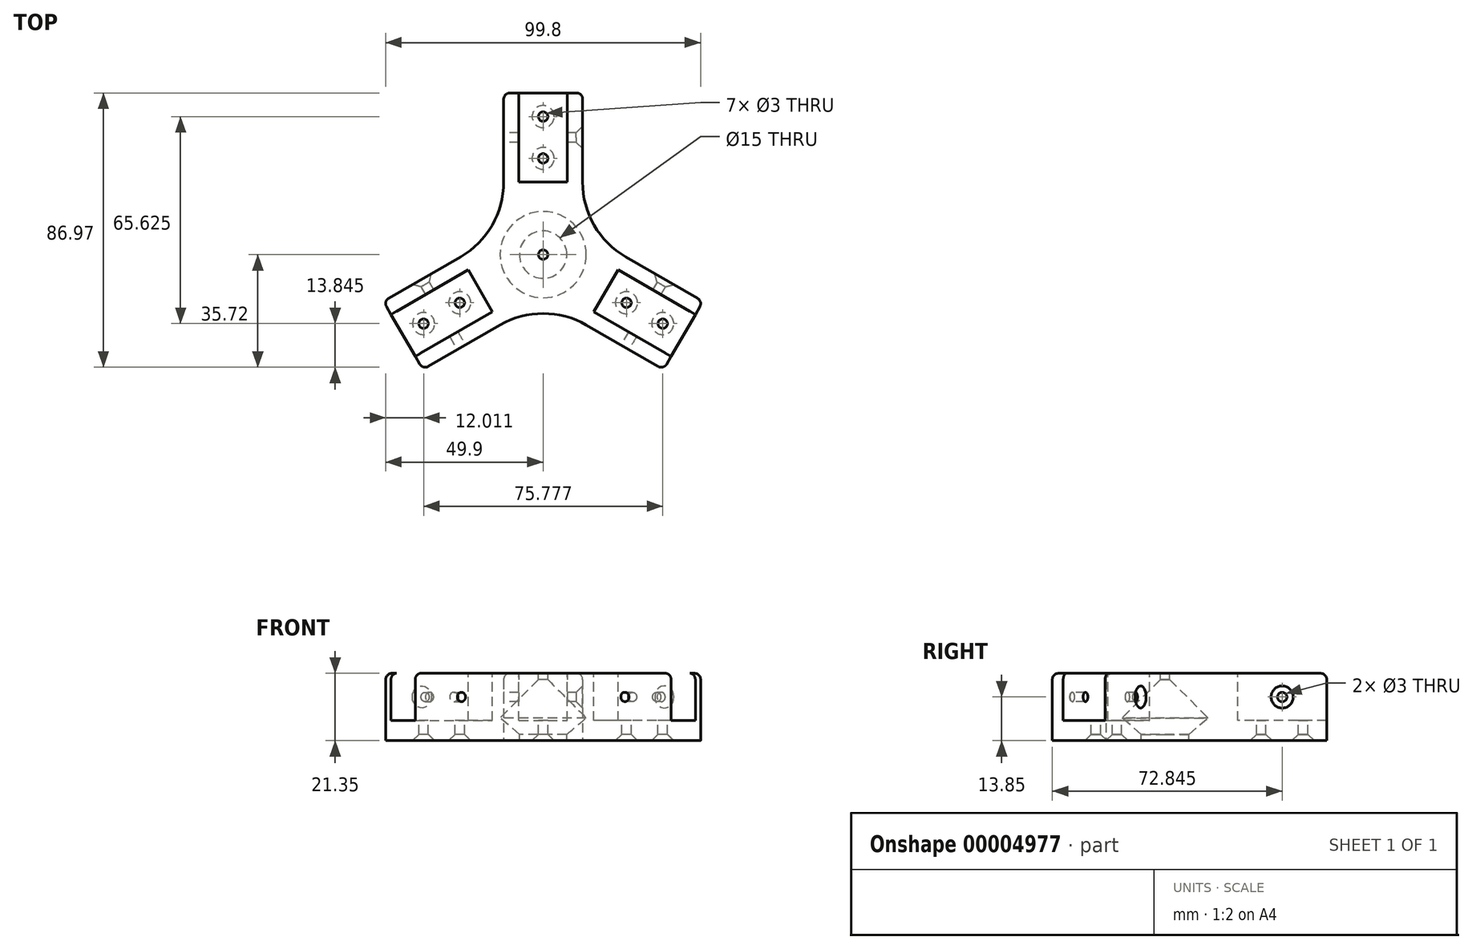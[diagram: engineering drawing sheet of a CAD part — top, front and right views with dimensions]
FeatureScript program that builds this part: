
annotation { "Feature Type Name" : "Feature", "Feature Type Description" : "" }
export const myFeature = defineFeature(function(context is Context, id is Id, definition is map)
    precondition{}
    {
        {
            var Q0;
            Q0=qCreatedBy(makeId("Top.planeOp"),FACE);
            var sketch = newSketch(context, id + "F0", { "sketchPlane" : qUnion([Q0])});
            skCircle(sketch, "E0", {"center": v(0, 0) * mm, "radius": 6.25 * mm, "construction": true});
            skLineSegment(sketch, "E1", {"start": v(0, 0) * mm, "end": v(0, 51.25) * mm, "construction": true});
            skLineSegment(sketch, "E2", {"start": v(-12.5, 51.25) * mm, "end": v(12.5, 51.25) * mm});
            skLineSegment(sketch, "E3", {"start": v(0, 0) * mm, "end": v(44.38, -25.62) * mm, "construction": true});
            skLineSegment(sketch, "E4", {"start": v(12.5, 51.25) * mm, "end": v(12.5, 23) * mm});
            skLineSegment(sketch, "E5", {"start": v(38.13, -36.45) * mm, "end": v(50.63, -14.8) * mm});
            skLineSegment(sketch, "E6", {"start": v(50.63, -14.8) * mm, "end": v(26.17, -0.67) * mm});
            skArc(sketch, "E7", {"start": v(12.5, 23) * mm, "mid": v(16.16, 9.33) * mm, "end": v(26.17, -0.67) * mm});
            skPoint(sketch, "E8", {"position": v(0, 6.25) * mm});
            skLineSegment(sketch, "E9.1.0", {"start": v(-50.63, -14.8) * mm, "end": v(-26.17, -0.67) * mm});
            skArc(sketch, "E9.1.1", {"start": v(-26.17, -0.67) * mm, "mid": v(-16.16, 9.33) * mm, "end": v(-12.5, 23) * mm});
            skLineSegment(sketch, "E9.1.2", {"start": v(-12.5, 51.25) * mm, "end": v(-12.5, 23) * mm});
            skLineSegment(sketch, "E9.2.0", {"start": v(38.13, -36.45) * mm, "end": v(13.67, -22.33) * mm});
            skArc(sketch, "E9.2.1", {"start": v(13.67, -22.33) * mm, "mid": v(0, -18.66) * mm, "end": v(-13.67, -22.33) * mm});
            skLineSegment(sketch, "E9.2.2", {"start": v(-38.13, -36.45) * mm, "end": v(-13.67, -22.33) * mm});
            skLineSegment(sketch, "E10", {"start": v(-50.63, -14.8) * mm, "end": v(-38.13, -36.45) * mm});
            skLineSegment(sketch, "E11", {"start": v(-12.5, 23) * mm, "end": v(12.5, 23) * mm, "construction": true});
            skCircle(sketch, "E12", {"center": v(0, 0) * mm, "radius": 13.66 * mm});
            skSolve(sketch);
        }
        {
            var Q0;
            Q0=qSketchRegion(id+"F0",true);
            extrude(context, id + "F1", {"entities" : qUnion([Q0]), "depth" : 21.35 * mm, "offsetDistance" : 25 * mm});
        }
        {
            var Q0;
            Q0=makeQuery(id+"F1.opExtrude","CAP_FACE",FACE,{"disambiguationData":[OSD([sQuery(id+"F0.wireOp",EDGE,"E0"),sQuery(id+"F0.wireOp",EDGE,"E2"),sQuery(id+"F0.wireOp",EDGE,"E4"),sQuery(id+"F0.wireOp",EDGE,"E5"),sQuery(id+"F0.wireOp",EDGE,"E6"),sQuery(id+"F0.wireOp",EDGE,"E7"),sQuery(id+"F0.wireOp",EDGE,"E9.1.0"),sQuery(id+"F0.wireOp",EDGE,"E9.1.1"),sQuery(id+"F0.wireOp",EDGE,"E9.1.2"),sQuery(id+"F0.wireOp",EDGE,"E9.2.0"),sQuery(id+"F0.wireOp",EDGE,"E9.2.1"),sQuery(id+"F0.wireOp",EDGE,"E9.2.2"),sQuery(id+"F0.wireOp",EDGE,"E10")])],"isStart":false});
            var sketch = newSketch(context, id + "F2", { "sketchPlane" : qUnion([Q0])});
            skLineSegment(sketch, "E13", {"start": v(0, 0) * mm, "end": v(0, 51.25) * mm, "construction": true});
            skLineSegment(sketch, "E14", {"start": v(-12.5, 23) * mm, "end": v(12.5, 23) * mm, "construction": true});
            skLineSegment(sketch, "E15.bottom", {"start": v(-7.68, 51.25) * mm, "end": v(7.67, 51.25) * mm});
            skLineSegment(sketch, "E15.top", {"start": v(-7.68, 23) * mm, "end": v(7.67, 23) * mm});
            skLineSegment(sketch, "E15.left", {"start": v(-7.68, 51.25) * mm, "end": v(-7.68, 23) * mm});
            skLineSegment(sketch, "E15.right", {"start": v(7.67, 51.25) * mm, "end": v(7.67, 23) * mm});
            skLineSegment(sketch, "E16.1.0", {"start": v(-48.22, -18.98) * mm, "end": v(-23.76, -4.85) * mm});
            skLineSegment(sketch, "E16.1.1", {"start": v(-40.55, -32.27) * mm, "end": v(-48.22, -18.98) * mm});
            skLineSegment(sketch, "E16.1.2", {"start": v(-40.55, -32.27) * mm, "end": v(-16.08, -18.15) * mm});
            skLineSegment(sketch, "E16.1.3", {"start": v(-16.08, -18.15) * mm, "end": v(-23.76, -4.85) * mm});
            skLineSegment(sketch, "E16.2.0", {"start": v(40.55, -32.27) * mm, "end": v(16.08, -18.15) * mm});
            skLineSegment(sketch, "E16.2.1", {"start": v(48.22, -18.98) * mm, "end": v(40.55, -32.27) * mm});
            skLineSegment(sketch, "E16.2.2", {"start": v(48.22, -18.98) * mm, "end": v(23.76, -4.85) * mm});
            skLineSegment(sketch, "E16.2.3", {"start": v(23.76, -4.85) * mm, "end": v(16.08, -18.15) * mm});
            skPoint(sketch, "E16.center", {"position": v(0, 0) * mm});
            skSolve(sketch);
        }
        {
            var Q0;
            Q0=qSketchRegion(id+"F2",true);
            extrude(context, id + "F3", {"entities" : qUnion([Q0]), "operationType" : NewBodyOperationType.REMOVE, "oppositeDirection" : true, "depth" : 15 * mm, "offsetDistance" : 25 * mm});
        }
        {
            var Q0;
            Q0=makeQuery(id+"F3.boolean.opBoolean","COPY",FACE,{"derivedFrom":makeQuery(id+"F3.opExtrude","CAP_FACE",FACE,{"disambiguationData":[OSD([sQuery(id+"F2.wireOp",EDGE,"E15.bottom"),sQuery(id+"F2.wireOp",EDGE,"E15.top"),sQuery(id+"F2.wireOp",EDGE,"E15.left"),sQuery(id+"F2.wireOp",EDGE,"E15.right")])],"isStart":false})});
            var sketch = newSketch(context, id + "F4", { "sketchPlane" : qUnion([Q0])});
            skLineSegment(sketch, "E17", {"start": v(0, 51.25) * mm, "end": v(0, 23) * mm, "construction": true});
            skCircle(sketch, "E18", {"center": v(0, 43.75) * mm, "radius": 1.5 * mm});
            skCircle(sketch, "E19", {"center": v(0, 30.5) * mm, "radius": 1.5 * mm});
            skCircle(sketch, "E20.1.0", {"center": v(-37.89, -21.87) * mm, "radius": 1.5 * mm});
            skCircle(sketch, "E20.1.1", {"center": v(-26.41, -15.25) * mm, "radius": 1.5 * mm});
            skCircle(sketch, "E20.2.0", {"center": v(37.89, -21.87) * mm, "radius": 1.5 * mm});
            skCircle(sketch, "E20.2.1", {"center": v(26.41, -15.25) * mm, "radius": 1.5 * mm});
            skPoint(sketch, "E20.center", {"position": v(0, 0) * mm});
            skSolve(sketch);
        }
        {
            var Q0;
            Q0=qSketchRegion(id+"F4",true);
            extrude(context, id + "F5", {"entities" : qUnion([Q0]), "operationType" : NewBodyOperationType.REMOVE, "endBound" : BoundingType.THROUGH_ALL, "oppositeDirection" : true, "depth" : 25 * mm});
        }
        {
            var Q0;
            {var subQ0=sQuery(id+"F0.wireOp",EDGE,"E2");var subQ1=sQuery(id+"F0.wireOp",EDGE,"E9.1.2");Q0=makeQuery(id+"F3.boolean.opBoolean","SPLIT",EDGE,{"disambiguationData":[TD([makeQuery(id+"F1.opExtrude","SWEPT_FACE",FACE,{"disambiguationData":[OSD([subQ1])]})])],"derivedFrom":makeQuery(id+"F1.opExtrude","CAP_EDGE",EDGE,{"disambiguationData":[OSD([subQ0])],"isStart":false})});}
            var Q1;
            {var subQ0=sQuery(id+"F0.wireOp",EDGE,"E2");var subQ1=sQuery(id+"F0.wireOp",EDGE,"E4");Q1=makeQuery(id+"F3.boolean.opBoolean","SPLIT",EDGE,{"disambiguationData":[TD([makeQuery(id+"F1.opExtrude","SWEPT_FACE",FACE,{"disambiguationData":[OSD([subQ1])]})])],"derivedFrom":makeQuery(id+"F1.opExtrude","CAP_EDGE",EDGE,{"disambiguationData":[OSD([subQ0])],"isStart":false})});}
            var Q2;
            {var subQ0=sQuery(id+"F0.wireOp",EDGE,"E5");var subQ1=sQuery(id+"F0.wireOp",EDGE,"E6");Q2=makeQuery(id+"F3.boolean.opBoolean","SPLIT",EDGE,{"disambiguationData":[TD([makeQuery(id+"F1.opExtrude","SWEPT_FACE",FACE,{"disambiguationData":[OSD([subQ1])]})])],"derivedFrom":makeQuery(id+"F1.opExtrude","CAP_EDGE",EDGE,{"disambiguationData":[OSD([subQ0])],"isStart":false})});}
            var Q3;
            {var subQ0=sQuery(id+"F0.wireOp",EDGE,"E5");var subQ1=sQuery(id+"F0.wireOp",EDGE,"E9.2.0");Q3=makeQuery(id+"F3.boolean.opBoolean","SPLIT",EDGE,{"disambiguationData":[TD([makeQuery(id+"F1.opExtrude","SWEPT_FACE",FACE,{"disambiguationData":[OSD([subQ1])]})])],"derivedFrom":makeQuery(id+"F1.opExtrude","CAP_EDGE",EDGE,{"disambiguationData":[OSD([subQ0])],"isStart":false})});}
            var Q4;
            {var subQ0=sQuery(id+"F0.wireOp",EDGE,"E10");var subQ1=sQuery(id+"F0.wireOp",EDGE,"E9.2.2");Q4=makeQuery(id+"F3.boolean.opBoolean","SPLIT",EDGE,{"disambiguationData":[TD([makeQuery(id+"F1.opExtrude","SWEPT_FACE",FACE,{"disambiguationData":[OSD([subQ1])]})])],"derivedFrom":makeQuery(id+"F1.opExtrude","CAP_EDGE",EDGE,{"disambiguationData":[OSD([subQ0])],"isStart":false})});}
            var Q5;
            {var subQ0=sQuery(id+"F0.wireOp",EDGE,"E10");var subQ1=sQuery(id+"F0.wireOp",EDGE,"E9.1.0");Q5=makeQuery(id+"F3.boolean.opBoolean","SPLIT",EDGE,{"disambiguationData":[TD([makeQuery(id+"F1.opExtrude","SWEPT_FACE",FACE,{"disambiguationData":[OSD([subQ1])]})])],"derivedFrom":makeQuery(id+"F1.opExtrude","CAP_EDGE",EDGE,{"disambiguationData":[OSD([subQ0])],"isStart":false})});}
            fillet(context, id + "F6", {"entities" : qUnion([Q0, Q1, Q2, Q3, Q4, Q5]), "radius" : 2 * mm, "tangentPropagation" : true, "allowEdgeOverflow" : false});
        }
        {
            var Q0;
            Q0=qCreatedBy(makeId("Front.planeOp"),FACE);
            var sketch = newSketch(context, id + "F7", { "sketchPlane" : qUnion([Q0])});
            skLineSegment(sketch, "E21.0", {"start": v(-13.66, 21.35) * mm, "end": v(13.66, 21.35) * mm, "construction": true});
            skLineSegment(sketch, "E22.0", {"start": v(-6.72, 0) * mm, "end": v(13.66, 0) * mm, "construction": true});
            skLineSegment(sketch, "E23", {"start": v(0, 21.35) * mm, "end": v(0, 0) * mm, "construction": true});
            skLineSegment(sketch, "E24", {"start": v(1.5, 21.35) * mm, "end": v(1.5, 19.35) * mm});
            skLineSegment(sketch, "E25", {"start": v(1.5, 19.35) * mm, "end": v(13.66, 7.19) * mm});
            skLineSegment(sketch, "E26", {"start": v(13.66, 7.19) * mm, "end": v(13.66, 21.35) * mm});
            skLineSegment(sketch, "E27", {"start": v(1.5, 21.35) * mm, "end": v(13.66, 21.35) * mm});
            skLineSegment(sketch, "E28", {"start": v(13.66, 0) * mm, "end": v(13.66, 7.19) * mm});
            skLineSegment(sketch, "E29", {"start": v(7.5, 2) * mm, "end": v(7.5, 0) * mm});
            skLineSegment(sketch, "E30", {"start": v(7.5, 0) * mm, "end": v(13.66, 0) * mm});
            skLineSegment(sketch, "E31.0", {"start": v(-13.66, 0) * mm, "end": v(13.66, 0) * mm, "construction": true});
            skLineSegment(sketch, "E32", {"start": v(13.66, 7.19) * mm, "end": v(7.5, 2) * mm});
            skSolve(sketch);
        }
        {
            var Q0;
            Q0 = qSketchRegion(id + "F7", true);
            var Q1;
            Q1=sQuery(id+"F7.wireOp",EDGE,"E23");
            revolve(context, id + "F8", {"operationType" : NewBodyOperationType.ADD, "entities" : qUnion([Q0]), "axis" : qUnion([Q1]), "revolveType" : RevolveType.FULL});
        }
        {
            var Q0;
            Q0=makeQuery(id+"F1.opExtrude","SWEPT_FACE",FACE,{"disambiguationData":[OSD([sQuery(id+"F0.wireOp",EDGE,"E9.2.2")])]});
            var sketch = newSketch(context, id + "F9", { "sketchPlane" : qUnion([Q0])});
            skLineSegment(sketch, "E33.0", {"start": v(-23, 6.35) * mm, "end": v(-23, 21.35) * mm, "construction": true});
            skLineSegment(sketch, "E34", {"start": v(-23, 13.85) * mm, "end": v(-51.25, 13.85) * mm, "construction": true});
            skCircle(sketch, "E35", {"center": v(-37.12, 13.85) * mm, "radius": 1.5 * mm});
            skSolve(sketch);
        }
        {
            var Q0;
            Q0 = qSketchRegion(id + "F9", true);
            extrude(context, id + "F10", {"entities" : qUnion([Q0]), "operationType" : NewBodyOperationType.REMOVE, "endBound" : BoundingType.THROUGH_ALL, "oppositeDirection" : true, "depth" : 25 * mm});
        }
        {
            var Q0;
            Q0=makeQuery(id+"F1.opExtrude","SWEPT_FACE",FACE,{"disambiguationData":[OSD([sQuery(id+"F0.wireOp",EDGE,"E9.2.0")])]});
            var sketch = newSketch(context, id + "F11", { "sketchPlane" : qUnion([Q0])});
            skLineSegment(sketch, "E36.0", {"start": v(23, 6.35) * mm, "end": v(23, 21.35) * mm, "construction": true});
            skLineSegment(sketch, "E37", {"start": v(23, 13.85) * mm, "end": v(51.25, 13.85) * mm, "construction": true});
            skCircle(sketch, "E38", {"center": v(37.12, 13.85) * mm, "radius": 1.5 * mm});
            skSolve(sketch);
        }
        {
            var Q0;
            Q0 = qSketchRegion(id + "F11", true);
            extrude(context, id + "F12", {"entities" : qUnion([Q0]), "operationType" : NewBodyOperationType.REMOVE, "endBound" : BoundingType.THROUGH_ALL, "oppositeDirection" : true, "depth" : 25 * mm});
        }
        {
            var Q0;
            Q0=makeQuery(id+"F1.opExtrude","SWEPT_FACE",FACE,{"disambiguationData":[OSD([sQuery(id+"F0.wireOp",EDGE,"E9.1.2")])]});
            var sketch = newSketch(context, id + "F13", { "sketchPlane" : qUnion([Q0])});
            skLineSegment(sketch, "E39.0", {"start": v(-23, 6.35) * mm, "end": v(-23, 21.35) * mm, "construction": true});
            skLineSegment(sketch, "E40", {"start": v(-23, 13.85) * mm, "end": v(-51.25, 13.85) * mm, "construction": true});
            skCircle(sketch, "E41", {"center": v(-37.13, 13.85) * mm, "radius": 1.5 * mm});
            skSolve(sketch);
        }
        {
            var Q0;
            Q0 = qSketchRegion(id + "F13", true);
            extrude(context, id + "F14", {"entities" : qUnion([Q0]), "operationType" : NewBodyOperationType.REMOVE, "endBound" : BoundingType.THROUGH_ALL, "oppositeDirection" : true, "depth" : 25 * mm});
        }
        {
            var Q0;
            Q0=makeQuery(id+"F1.opExtrude","SWEPT_EDGE",EDGE,{"disambiguationData":[OSD([sQuery(id+"F0.wireOp",EDGE,"E9.2.2"),sQuery(id+"F0.wireOp",EDGE,"E10")])]});
            var Q1;
            Q1=makeQuery(id+"F1.opExtrude","SWEPT_EDGE",EDGE,{"disambiguationData":[OSD([sQuery(id+"F0.wireOp",EDGE,"E9.1.0"),sQuery(id+"F0.wireOp",EDGE,"E10")])]});
            var Q2;
            Q2=makeQuery(id+"F1.opExtrude","SWEPT_EDGE",EDGE,{"disambiguationData":[OSD([sQuery(id+"F0.wireOp",EDGE,"E5"),sQuery(id+"F0.wireOp",EDGE,"E6")])]});
            fillet(context, id + "F15", {"entities" : qUnion([Q0, Q1, Q2]), "radius" : 2 * mm, "tangentPropagation" : true, "defaultsChanged" : true, "vertexSettings" : [], "allowEdgeOverflow" : false});
        }
        {
            var Q0;
            Q0=makeQuery(id+"F5.boolean.opBoolean","INTERSECT",EDGE,{"derivedFrom":[makeQuery(id+"F1.opExtrude","CAP_FACE",FACE,{"disambiguationData":[OSD([sQuery(id+"F0.wireOp",EDGE,"E2"),sQuery(id+"F0.wireOp",EDGE,"E4"),sQuery(id+"F0.wireOp",EDGE,"E5"),sQuery(id+"F0.wireOp",EDGE,"E6"),sQuery(id+"F0.wireOp",EDGE,"E7"),sQuery(id+"F0.wireOp",EDGE,"E9.1.0"),sQuery(id+"F0.wireOp",EDGE,"E9.1.1"),sQuery(id+"F0.wireOp",EDGE,"E9.1.2"),sQuery(id+"F0.wireOp",EDGE,"E9.2.0"),sQuery(id+"F0.wireOp",EDGE,"E9.2.1"),sQuery(id+"F0.wireOp",EDGE,"E9.2.2"),sQuery(id+"F0.wireOp",EDGE,"E10"),sQuery(id+"F0.wireOp",EDGE,"E12")])],"isStart":true}),makeQuery(id+"F5.opExtrude","SWEPT_FACE",FACE,{"disambiguationData":[OSD([sQuery(id+"F4.wireOp",EDGE,"E20.2.0")])]})]});
            var Q1;
            Q1=makeQuery(id+"F5.boolean.opBoolean","INTERSECT",EDGE,{"derivedFrom":[makeQuery(id+"F1.opExtrude","CAP_FACE",FACE,{"disambiguationData":[OSD([sQuery(id+"F0.wireOp",EDGE,"E2"),sQuery(id+"F0.wireOp",EDGE,"E4"),sQuery(id+"F0.wireOp",EDGE,"E5"),sQuery(id+"F0.wireOp",EDGE,"E6"),sQuery(id+"F0.wireOp",EDGE,"E7"),sQuery(id+"F0.wireOp",EDGE,"E9.1.0"),sQuery(id+"F0.wireOp",EDGE,"E9.1.1"),sQuery(id+"F0.wireOp",EDGE,"E9.1.2"),sQuery(id+"F0.wireOp",EDGE,"E9.2.0"),sQuery(id+"F0.wireOp",EDGE,"E9.2.1"),sQuery(id+"F0.wireOp",EDGE,"E9.2.2"),sQuery(id+"F0.wireOp",EDGE,"E10"),sQuery(id+"F0.wireOp",EDGE,"E12")])],"isStart":true}),makeQuery(id+"F5.opExtrude","SWEPT_FACE",FACE,{"disambiguationData":[OSD([sQuery(id+"F4.wireOp",EDGE,"E20.2.1")])]})]});
            var Q2;
            Q2=makeQuery(id+"F5.boolean.opBoolean","INTERSECT",EDGE,{"derivedFrom":[makeQuery(id+"F1.opExtrude","CAP_FACE",FACE,{"disambiguationData":[OSD([sQuery(id+"F0.wireOp",EDGE,"E2"),sQuery(id+"F0.wireOp",EDGE,"E4"),sQuery(id+"F0.wireOp",EDGE,"E5"),sQuery(id+"F0.wireOp",EDGE,"E6"),sQuery(id+"F0.wireOp",EDGE,"E7"),sQuery(id+"F0.wireOp",EDGE,"E9.1.0"),sQuery(id+"F0.wireOp",EDGE,"E9.1.1"),sQuery(id+"F0.wireOp",EDGE,"E9.1.2"),sQuery(id+"F0.wireOp",EDGE,"E9.2.0"),sQuery(id+"F0.wireOp",EDGE,"E9.2.1"),sQuery(id+"F0.wireOp",EDGE,"E9.2.2"),sQuery(id+"F0.wireOp",EDGE,"E10"),sQuery(id+"F0.wireOp",EDGE,"E12")])],"isStart":true}),makeQuery(id+"F5.opExtrude","SWEPT_FACE",FACE,{"disambiguationData":[OSD([sQuery(id+"F4.wireOp",EDGE,"E20.1.1")])]})]});
            var Q3;
            Q3=makeQuery(id+"F5.boolean.opBoolean","INTERSECT",EDGE,{"derivedFrom":[makeQuery(id+"F1.opExtrude","CAP_FACE",FACE,{"disambiguationData":[OSD([sQuery(id+"F0.wireOp",EDGE,"E2"),sQuery(id+"F0.wireOp",EDGE,"E4"),sQuery(id+"F0.wireOp",EDGE,"E5"),sQuery(id+"F0.wireOp",EDGE,"E6"),sQuery(id+"F0.wireOp",EDGE,"E7"),sQuery(id+"F0.wireOp",EDGE,"E9.1.0"),sQuery(id+"F0.wireOp",EDGE,"E9.1.1"),sQuery(id+"F0.wireOp",EDGE,"E9.1.2"),sQuery(id+"F0.wireOp",EDGE,"E9.2.0"),sQuery(id+"F0.wireOp",EDGE,"E9.2.1"),sQuery(id+"F0.wireOp",EDGE,"E9.2.2"),sQuery(id+"F0.wireOp",EDGE,"E10"),sQuery(id+"F0.wireOp",EDGE,"E12")])],"isStart":true}),makeQuery(id+"F5.opExtrude","SWEPT_FACE",FACE,{"disambiguationData":[OSD([sQuery(id+"F4.wireOp",EDGE,"E20.1.0")])]})]});
            var Q4;
            Q4=makeQuery(id+"F5.boolean.opBoolean","INTERSECT",EDGE,{"derivedFrom":[makeQuery(id+"F1.opExtrude","CAP_FACE",FACE,{"disambiguationData":[OSD([sQuery(id+"F0.wireOp",EDGE,"E2"),sQuery(id+"F0.wireOp",EDGE,"E4"),sQuery(id+"F0.wireOp",EDGE,"E5"),sQuery(id+"F0.wireOp",EDGE,"E6"),sQuery(id+"F0.wireOp",EDGE,"E7"),sQuery(id+"F0.wireOp",EDGE,"E9.1.0"),sQuery(id+"F0.wireOp",EDGE,"E9.1.1"),sQuery(id+"F0.wireOp",EDGE,"E9.1.2"),sQuery(id+"F0.wireOp",EDGE,"E9.2.0"),sQuery(id+"F0.wireOp",EDGE,"E9.2.1"),sQuery(id+"F0.wireOp",EDGE,"E9.2.2"),sQuery(id+"F0.wireOp",EDGE,"E10"),sQuery(id+"F0.wireOp",EDGE,"E12")])],"isStart":true}),makeQuery(id+"F5.opExtrude","SWEPT_FACE",FACE,{"disambiguationData":[OSD([sQuery(id+"F4.wireOp",EDGE,"E19")])]})]});
            var Q5;
            Q5=makeQuery(id+"F5.boolean.opBoolean","INTERSECT",EDGE,{"derivedFrom":[makeQuery(id+"F1.opExtrude","CAP_FACE",FACE,{"disambiguationData":[OSD([sQuery(id+"F0.wireOp",EDGE,"E2"),sQuery(id+"F0.wireOp",EDGE,"E4"),sQuery(id+"F0.wireOp",EDGE,"E5"),sQuery(id+"F0.wireOp",EDGE,"E6"),sQuery(id+"F0.wireOp",EDGE,"E7"),sQuery(id+"F0.wireOp",EDGE,"E9.1.0"),sQuery(id+"F0.wireOp",EDGE,"E9.1.1"),sQuery(id+"F0.wireOp",EDGE,"E9.1.2"),sQuery(id+"F0.wireOp",EDGE,"E9.2.0"),sQuery(id+"F0.wireOp",EDGE,"E9.2.1"),sQuery(id+"F0.wireOp",EDGE,"E9.2.2"),sQuery(id+"F0.wireOp",EDGE,"E10"),sQuery(id+"F0.wireOp",EDGE,"E12")])],"isStart":true}),makeQuery(id+"F5.opExtrude","SWEPT_FACE",FACE,{"disambiguationData":[OSD([sQuery(id+"F4.wireOp",EDGE,"E18")])]})]});
            var Q6;
            Q6=makeQuery(id+"F12.boolean.opBoolean","INTERSECT",EDGE,{"derivedFrom":[makeQuery(id+"F1.opExtrude","SWEPT_FACE",FACE,{"disambiguationData":[OSD([sQuery(id+"F0.wireOp",EDGE,"E6")])]}),makeQuery(id+"F12.opExtrude","SWEPT_FACE",FACE,{"disambiguationData":[OSD([sQuery(id+"F11.wireOp",EDGE,"E38")])]})]});
            var Q7;
            Q7=makeQuery(id+"F14.boolean.opBoolean","INTERSECT",EDGE,{"derivedFrom":[makeQuery(id+"F1.opExtrude","SWEPT_FACE",FACE,{"disambiguationData":[OSD([sQuery(id+"F0.wireOp",EDGE,"E4")])]}),makeQuery(id+"F14.opExtrude","SWEPT_FACE",FACE,{"disambiguationData":[OSD([sQuery(id+"F13.wireOp",EDGE,"E41")])]})]});
            var Q8;
            Q8=makeQuery(id+"F12.boolean.opBoolean","COPY",EDGE,{"derivedFrom":makeQuery(id+"F12.opExtrude","CAP_EDGE",EDGE,{"disambiguationData":[OSD([sQuery(id+"F11.wireOp",EDGE,"E38")])],"isStart":true})});
            var Q9;
            Q9=makeQuery(id+"F10.boolean.opBoolean","COPY",EDGE,{"derivedFrom":makeQuery(id+"F10.opExtrude","CAP_EDGE",EDGE,{"disambiguationData":[OSD([sQuery(id+"F9.wireOp",EDGE,"E35")])],"isStart":true})});
            var Q10;
            Q10=makeQuery(id+"F10.boolean.opBoolean","INTERSECT",EDGE,{"derivedFrom":[makeQuery(id+"F1.opExtrude","SWEPT_FACE",FACE,{"disambiguationData":[OSD([sQuery(id+"F0.wireOp",EDGE,"E9.1.0")])]}),makeQuery(id+"F10.opExtrude","SWEPT_FACE",FACE,{"disambiguationData":[OSD([sQuery(id+"F9.wireOp",EDGE,"E35")])]})]});
            var Q11;
            Q11=makeQuery(id+"F14.boolean.opBoolean","COPY",EDGE,{"derivedFrom":makeQuery(id+"F14.opExtrude","CAP_EDGE",EDGE,{"disambiguationData":[OSD([sQuery(id+"F13.wireOp",EDGE,"E41")])],"isStart":true})});
            chamfer(context, id + "F16", {"entities" : qUnion([Q0, Q1, Q2, Q3, Q4, Q5, Q6, Q7, Q8, Q9, Q10, Q11]), "width" : 2 * mm, "tangentPropagation" : true});
        }
    });
